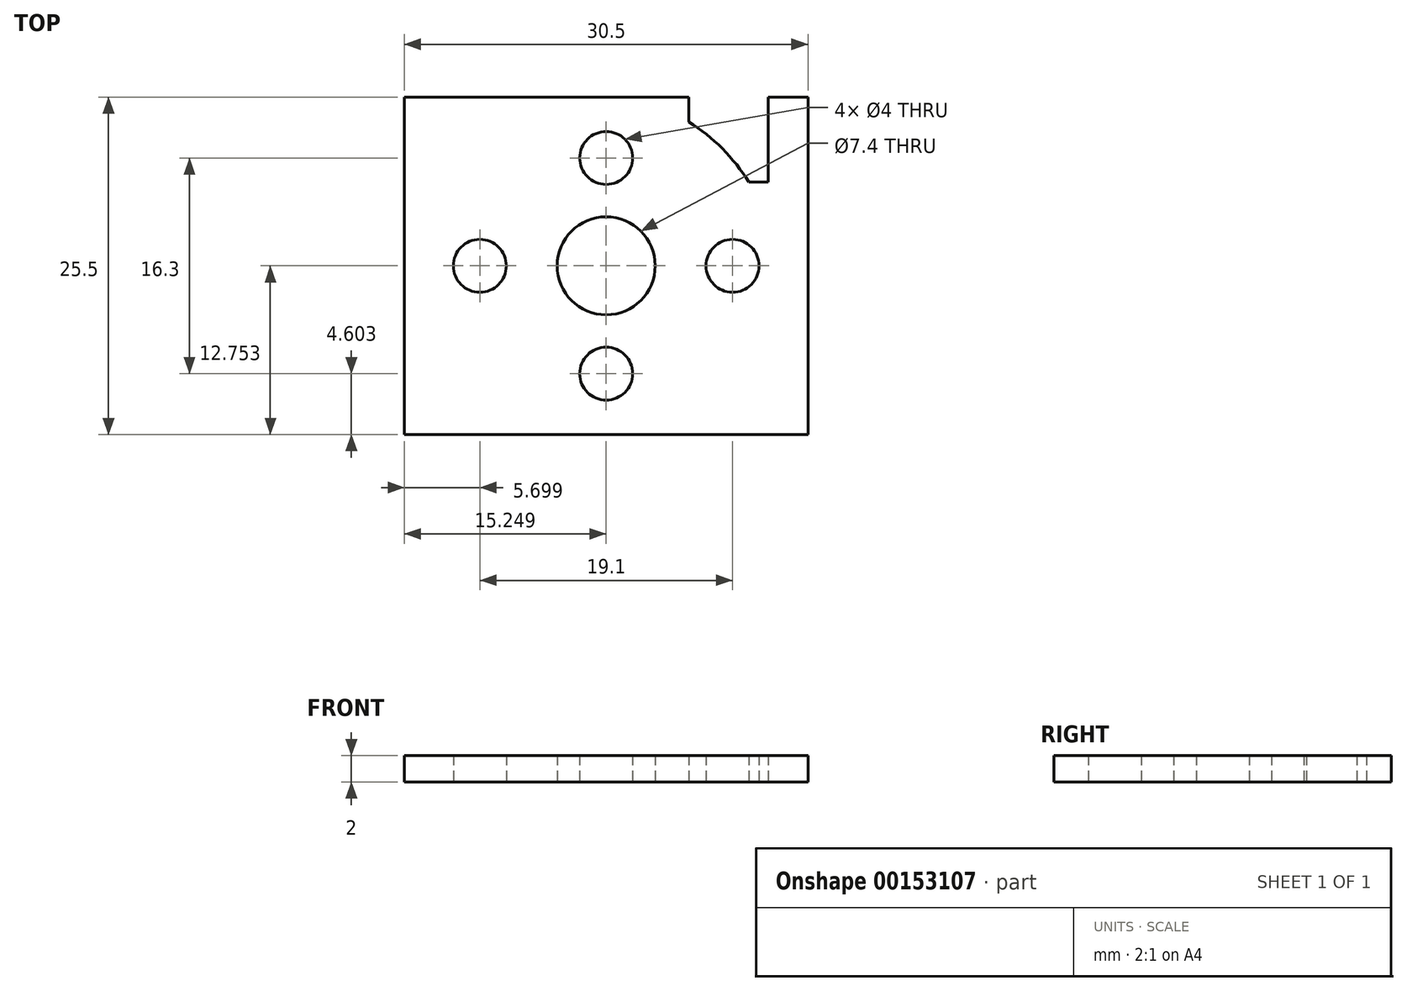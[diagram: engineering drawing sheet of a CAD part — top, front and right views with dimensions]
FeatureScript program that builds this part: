
annotation { "Feature Type Name" : "Feature", "Feature Type Description" : "" }
export const myFeature = defineFeature(function(context is Context, id is Id, definition is map)
    precondition{}
    {
        {
            var Q0;
            Q0=qCreatedBy(makeId("Top.planeOp"),FACE);
            var sketch = newSketch(context, id + "F0", { "sketchPlane" : qUnion([Q0])});
            skLineSegment(sketch, "E0.top", {"start": v(-46, 10.64) * mm, "end": v(-15.5, 10.64) * mm});
            skLineSegment(sketch, "E0.left", {"start": v(-46, 36.14) * mm, "end": v(-46, 10.64) * mm});
            skLineSegment(sketch, "E0.right", {"start": v(-15.5, 36.14) * mm, "end": v(-15.5, 10.64) * mm});
            skLineSegment(sketch, "E1", {"start": v(-30.75, 36.14) * mm, "end": v(-30.75, 10.64) * mm, "construction": true});
            skLineSegment(sketch, "E2", {"start": v(-46, 23.4) * mm, "end": v(-15.5, 23.4) * mm, "construction": true});
            skCircle(sketch, "E3", {"center": v(-30.75, 23.4) * mm, "radius": 3.7 * mm});
            skLineSegment(sketch, "E4.bottom", {"start": v(-46, 10.64) * mm, "end": v(-37, 10.64) * mm, "construction": true});
            skLineSegment(sketch, "E4.left", {"start": v(-46, 10.64) * mm, "end": v(-46, 19.64) * mm, "construction": true});
            skLineSegment(sketch, "E5.left", {"start": v(-15.5, 36.14) * mm, "end": v(-15.5, 32.4) * mm, "construction": true});
            skLineSegment(sketch, "E5.right", {"start": v(-24.5, 36.14) * mm, "end": v(-24.5, 34.22) * mm, "construction": true});
            skLineSegment(sketch, "E6", {"start": v(-46, 36.14) * mm, "end": v(-24.5, 36.14) * mm});
            skCircle(sketch, "E7", {"center": v(-30.75, 23.4) * mm, "radius": 9.55 * mm, "construction": true});
            skCircle(sketch, "E8", {"center": v(-40.3, 23.4) * mm, "radius": 2 * mm});
            skCircle(sketch, "E9", {"center": v(-21.2, 23.4) * mm, "radius": 2 * mm});
            skCircle(sketch, "E10", {"center": v(-30.75, 23.4) * mm, "radius": 8.15 * mm, "construction": true});
            skCircle(sketch, "E11", {"center": v(-30.75, 31.54) * mm, "radius": 2 * mm});
            skCircle(sketch, "E12", {"center": v(-30.75, 15.24) * mm, "radius": 2 * mm});
            skLineSegment(sketch, "E13", {"start": v(-24.5, 36.14) * mm, "end": v(-24.5, 34.22) * mm});
            skLineSegment(sketch, "E14", {"start": v(-15.5, 36.14) * mm, "end": v(-18.5, 36.14) * mm});
            skLineSegment(sketch, "E15", {"start": v(-18.5, 36.14) * mm, "end": v(-18.5, 29.72) * mm});
            skLineSegment(sketch, "E16", {"start": v(-15.5, 36.14) * mm, "end": v(-24.5, 36.14) * mm, "construction": true});
            skLineSegment(sketch, "E17", {"start": v(-19.97, 29.72) * mm, "end": v(-18.5, 29.72) * mm});
            skCircle(sketch, "E18", {"center": v(-30.75, 23.4) * mm, "radius": 12.5 * mm, "construction": true});
            skArc(sketch, "E19", {"start": v(-19.97, 29.72) * mm, "mid": v(-21.98, 32.25) * mm, "end": v(-24.5, 34.27) * mm});
            skLineSegment(sketch, "E20", {"start": v(-30.75, 23.4) * mm, "end": v(-51.2, 14.92) * mm, "construction": true});
            skLineSegment(sketch, "E21", {"start": v(-39.09, 3.27) * mm, "end": v(-30.75, 23.4) * mm, "construction": true});
            skSolve(sketch);
        }
        {
            var Q0;
            Q0=makeQuery(id+"F0.imprint","IMPRINT",FACE,{"disambiguationData":[TD([[makeQuery(id+"F0.imprint","IMPRINT",EDGE,{"derivedFrom":sQuery(id+"F0.wireOp",EDGE,"E0.top")}),1.0]])]});
            extrude(context, id + "F1", {"entities" : qUnion([Q0]), "depth" : 2 * mm});
        }
    });
